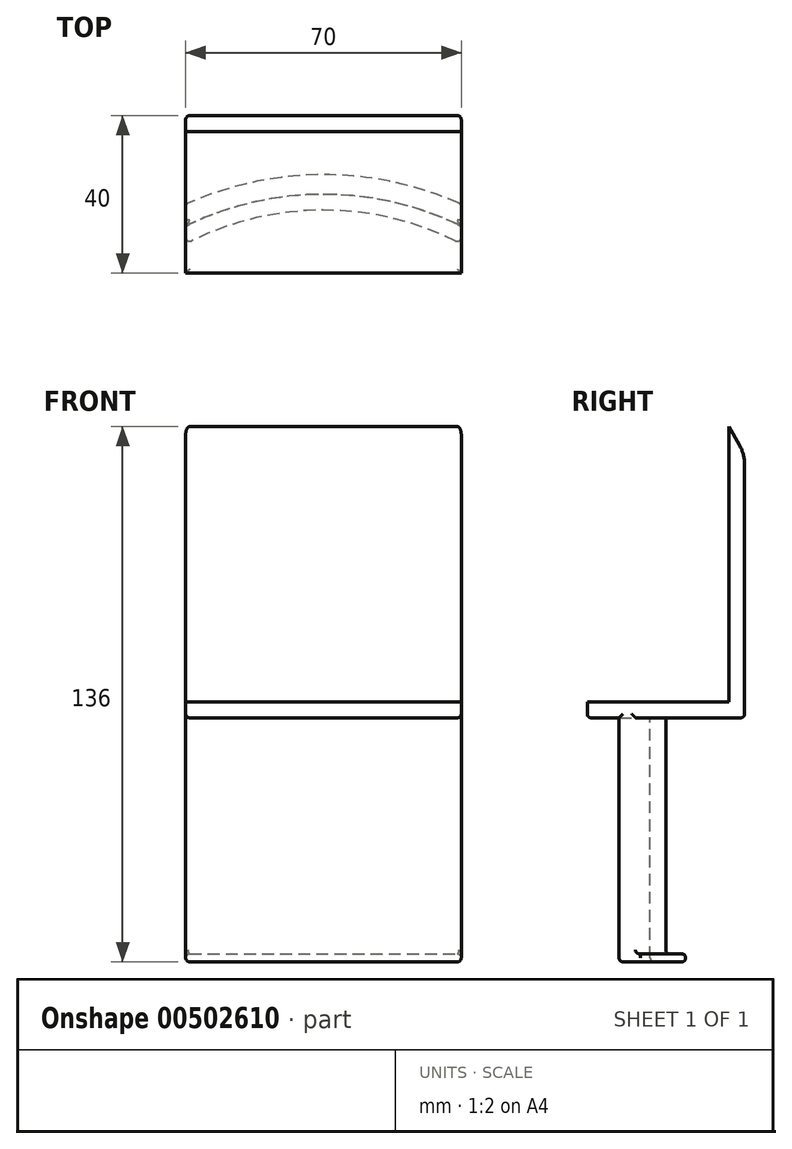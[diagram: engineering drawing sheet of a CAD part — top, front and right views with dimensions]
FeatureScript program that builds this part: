
annotation { "Feature Type Name" : "Feature", "Feature Type Description" : "" }
export const myFeature = defineFeature(function(context is Context, id is Id, definition is map)
    precondition{}
    {
        {
            var Q0;
            Q0=qCreatedBy(makeId("Top.planeOp"),FACE);
            var sketch = newSketch(context, id + "F0", { "sketchPlane" : qUnion([Q0])});
            skLineSegment(sketch, "E0.bottom", {"start": v(-35, 0) * mm, "end": v(35, 0) * mm});
            skLineSegment(sketch, "E0.top", {"start": v(-35, 4) * mm, "end": v(35, 4) * mm});
            skLineSegment(sketch, "E0.left", {"start": v(-35, 0) * mm, "end": v(-35, 4) * mm});
            skLineSegment(sketch, "E0.right", {"start": v(35, 0) * mm, "end": v(35, 4) * mm});
            skSolve(sketch);
        }
        {
            var Q0;
            Q0 = qSketchRegion(id + "F0", true);
            extrude(context, id + "F1", {"entities" : qUnion([Q0]), "depth" : 70 * mm});
        }
        {
            var Q0;
            Q0=makeQuery(id+"F1.opExtrude","CAP_EDGE",EDGE,{"disambiguationData":[OSD([sQuery(id+"F0.wireOp",EDGE,"E0.top")])],"isStart":false});
            chamfer(context, id + "F2", {"entities" : qUnion([Q0]), "chamferType" : ChamferType.TWO_OFFSETS, "width1" : 7 * mm, "oppositeDirection" : false, "width2" : 4 * mm, "tangentPropagation" : true});
        }
        {
            var Q0;
            {var subQ0=sQuery(id+"F0.wireOp",EDGE,"E0.top");Q0=makeQuery(id+"F2.opChamfer","BLEND_EDGE",EDGE,{"blendedFrom":[makeQuery(id+"F1.opExtrude","CAP_EDGE",EDGE,{"disambiguationData":[OSD([subQ0])],"isStart":false}),makeQuery(id+"F1.opExtrude","SWEPT_FACE",FACE,{"disambiguationData":[OSD([subQ0])]})],"blendedInto":[makeQuery(id+"F1.opExtrude","SWEPT_FACE",FACE,{"disambiguationData":[OSD([subQ0])]})]});}
            fillet(context, id + "F3", {"entities" : qUnion([Q0]), "radius" : 10 * mm, "tangentPropagation" : true, "allowEdgeOverflow" : false});
        }
        {
            var Q0;
            Q0=qCreatedBy(makeId("Top.planeOp"),FACE);
            var sketch = newSketch(context, id + "F4", { "sketchPlane" : qUnion([Q0])});
            skPoint(sketch, "E1.0", {"position": v(-35, 4) * mm});
            skPoint(sketch, "E1.1", {"position": v(35, 4) * mm});
            skLineSegment(sketch, "E2.bottom", {"start": v(-35, 4) * mm, "end": v(35, 4) * mm});
            skLineSegment(sketch, "E2.top", {"start": v(-35, -36) * mm, "end": v(35, -36) * mm});
            skLineSegment(sketch, "E2.left", {"start": v(-35, 4) * mm, "end": v(-35, -36) * mm});
            skLineSegment(sketch, "E2.right", {"start": v(35, 4) * mm, "end": v(35, -36) * mm});
            skSolve(sketch);
        }
        {
            var Q0;
            Q0 = qSketchRegion(id + "F4", true);
            extrude(context, id + "F5", {"entities" : qUnion([Q0]), "operationType" : NewBodyOperationType.ADD, "oppositeDirection" : true, "depth" : 4 * mm});
        }
        {
            var Q0;
            Q0=makeQuery(id+"F5.opExtrude","CAP_FACE",FACE,{"disambiguationData":[OSD([sQuery(id+"F4.wireOp",EDGE,"E2.bottom"),sQuery(id+"F4.wireOp",EDGE,"E2.top"),sQuery(id+"F4.wireOp",EDGE,"E2.left"),sQuery(id+"F4.wireOp",EDGE,"E2.right")])],"isStart":false});
            var sketch = newSketch(context, id + "F6", { "sketchPlane" : qUnion([Q0])});
            skArc(sketch, "E3", {"start": v(-35, 24.06) * mm, "mid": v(0, 16) * mm, "end": v(35, 24.06) * mm});
            skArc(sketch, "E4", {"start": v(-35, 28.54) * mm, "mid": v(0, 20) * mm, "end": v(35, 28.54) * mm});
            skLineSegment(sketch, "E5", {"start": v(-35, 28.54) * mm, "end": v(-35, 24.06) * mm});
            skLineSegment(sketch, "E6", {"start": v(35, 28.54) * mm, "end": v(35, 24.06) * mm});
            skSolve(sketch);
        }
        {
            var Q0;
            Q0 = qSketchRegion(id + "F6", true);
            extrude(context, id + "F7", {"entities" : qUnion([Q0]), "operationType" : NewBodyOperationType.ADD, "depth" : 60 * mm});
        }
        {
            var Q0;
            Q0=makeQuery(id+"F7.opExtrude","CAP_FACE",FACE,{"disambiguationData":[OSD([sQuery(id+"F6.wireOp",EDGE,"E3"),sQuery(id+"F6.wireOp",EDGE,"E4"),sQuery(id+"F6.wireOp",EDGE,"E5"),sQuery(id+"F6.wireOp",EDGE,"E6")])],"isStart":false});
            var sketch = newSketch(context, id + "F8", { "sketchPlane" : qUnion([Q0])});
            skArc(sketch, "E7", {"start": v(-35, 18.54) * mm, "mid": v(0, 11) * mm, "end": v(35, 18.54) * mm});
            skLineSegment(sketch, "E8", {"start": v(-35, 24.06) * mm, "end": v(-35, 18.54) * mm});
            skLineSegment(sketch, "E9", {"start": v(35, 24.06) * mm, "end": v(35, 18.54) * mm});
            skLineSegment(sketch, "E10.0", {"start": v(-35, 28.54) * mm, "end": v(-35, 24.06) * mm});
            skArc(sketch, "E10.1", {"start": v(-35, 28.54) * mm, "mid": v(0, 20) * mm, "end": v(35, 28.54) * mm});
            skLineSegment(sketch, "E10.2", {"start": v(35, 28.54) * mm, "end": v(35, 24.06) * mm});
            skSolve(sketch);
        }
        {
            var Q0;
            Q0 = qSketchRegion(id + "F8", true);
            extrude(context, id + "F9", {"entities" : qUnion([Q0]), "operationType" : NewBodyOperationType.ADD, "depth" : 2 * mm});
        }
        {
            var Q0;
            Q0=makeQuery(id+"F7.opExtrude","CAP_EDGE",EDGE,{"disambiguationData":[OSD([sQuery(id+"F6.wireOp",EDGE,"E3")])],"isStart":false});
            var Q1;
            Q1=makeQuery(id+"F7.opExtrude","CAP_EDGE",EDGE,{"disambiguationData":[OSD([sQuery(id+"F6.wireOp",EDGE,"E3")])],"isStart":true});
            var Q2;
            Q2=makeQuery(id+"F5.opExtrude","CAP_EDGE",EDGE,{"disambiguationData":[OSD([sQuery(id+"F4.wireOp",EDGE,"E2.right")])],"isStart":false});
            var Q3;
            Q3=makeQuery(id+"F5.opExtrude","CAP_EDGE",EDGE,{"disambiguationData":[OSD([sQuery(id+"F4.wireOp",EDGE,"E2.left")])],"isStart":false});
            var Q4;
            Q4=makeQuery(id+"F5.opExtrude","CAP_EDGE",EDGE,{"disambiguationData":[OSD([sQuery(id+"F4.wireOp",EDGE,"E2.top")])],"isStart":false});
            var Q5;
            Q5=makeQuery(id+"F9.opExtrude","CAP_EDGE",EDGE,{"disambiguationData":[OSD([sQuery(id+"F8.wireOp",EDGE,"E10.1")])],"isStart":false});
            var Q6;
            Q6=makeQuery(id+"F9.boolean.opBoolean","MERGE",EDGE,{"derivedFrom":[makeQuery(id+"F7.opExtrude","SWEPT_EDGE",EDGE,{"disambiguationData":[OSD([sQuery(id+"F6.wireOp",EDGE,"E4"),sQuery(id+"F6.wireOp",EDGE,"E6")])]}),makeQuery(id+"F9.opExtrude","SWEPT_EDGE",EDGE,{"disambiguationData":[OSD([sQuery(id+"F8.wireOp",EDGE,"E10.1"),sQuery(id+"F8.wireOp",EDGE,"E10.2")])]})]});
            var Q7;
            Q7=makeQuery(id+"F9.boolean.opBoolean","MERGE",EDGE,{"derivedFrom":[makeQuery(id+"F7.opExtrude","SWEPT_EDGE",EDGE,{"disambiguationData":[OSD([sQuery(id+"F6.wireOp",EDGE,"E4"),sQuery(id+"F6.wireOp",EDGE,"E5")])]}),makeQuery(id+"F9.opExtrude","SWEPT_EDGE",EDGE,{"disambiguationData":[OSD([sQuery(id+"F8.wireOp",EDGE,"E10.0"),sQuery(id+"F8.wireOp",EDGE,"E10.1")])]})]});
            var Q8;
            Q8=makeQuery(id+"F7.opExtrude","SWEPT_EDGE",EDGE,{"disambiguationData":[OSD([sQuery(id+"F6.wireOp",EDGE,"E3"),sQuery(id+"F6.wireOp",EDGE,"E5")])]});
            var Q9;
            Q9=makeQuery(id+"F7.opExtrude","SWEPT_EDGE",EDGE,{"disambiguationData":[OSD([sQuery(id+"F6.wireOp",EDGE,"E3"),sQuery(id+"F6.wireOp",EDGE,"E6")])]});
            var Q10;
            Q10=makeQuery(id+"F9.opExtrude","CAP_EDGE",EDGE,{"disambiguationData":[OSD([sQuery(id+"F8.wireOp",EDGE,"E7")])],"isStart":false});
            var Q11;
            Q11=makeQuery(id+"F9.opExtrude","CAP_EDGE",EDGE,{"disambiguationData":[OSD([sQuery(id+"F8.wireOp",EDGE,"E7")])],"isStart":true});
            var Q12;
            Q12=makeQuery(id+"F9.opExtrude","CAP_EDGE",EDGE,{"disambiguationData":[OSD([sQuery(id+"F8.wireOp",EDGE,"E9"),sQuery(id+"F8.wireOp",EDGE,"E10.2")])],"isStart":false});
            var Q13;
            Q13=makeQuery(id+"F9.opExtrude","CAP_EDGE",EDGE,{"disambiguationData":[OSD([sQuery(id+"F8.wireOp",EDGE,"E8"),sQuery(id+"F8.wireOp",EDGE,"E10.0")])],"isStart":false});
            var Q14;
            Q14=makeQuery(id+"F9.opExtrude","CAP_EDGE",EDGE,{"disambiguationData":[OSD([sQuery(id+"F8.wireOp",EDGE,"E8"),sQuery(id+"F8.wireOp",EDGE,"E10.0")])],"isStart":true});
            var Q15;
            Q15=makeQuery(id+"F9.opExtrude","SWEPT_EDGE",EDGE,{"disambiguationData":[OSD([sQuery(id+"F8.wireOp",EDGE,"E7"),sQuery(id+"F8.wireOp",EDGE,"E9")])]});
            var Q16;
            Q16=makeQuery(id+"F9.opExtrude","CAP_EDGE",EDGE,{"disambiguationData":[OSD([sQuery(id+"F8.wireOp",EDGE,"E9"),sQuery(id+"F8.wireOp",EDGE,"E10.2")])],"isStart":true});
            var Q17;
            Q17=makeQuery(id+"F9.opExtrude","SWEPT_EDGE",EDGE,{"disambiguationData":[OSD([sQuery(id+"F8.wireOp",EDGE,"E7"),sQuery(id+"F8.wireOp",EDGE,"E8")])]});
            var Q18;
            Q18=makeQuery(id+"F5.opExtrude","CAP_EDGE",EDGE,{"disambiguationData":[OSD([sQuery(id+"F4.wireOp",EDGE,"E2.bottom")])],"isStart":false});
            var Q19;
            Q19=makeQuery(id+"F5.boolean.opBoolean","MERGE",EDGE,{"derivedFrom":[makeQuery(id+"F1.opExtrude","SWEPT_EDGE",EDGE,{"disambiguationData":[OSD([sQuery(id+"F0.wireOp",EDGE,"E0.top"),sQuery(id+"F0.wireOp",EDGE,"E0.right")])]}),makeQuery(id+"F5.opExtrude","SWEPT_EDGE",EDGE,{"disambiguationData":[OSD([sQuery(id+"F4.wireOp",EDGE,"E2.bottom"),sQuery(id+"F4.wireOp",EDGE,"E2.right")])]})]});
            var Q20;
            Q20=makeQuery(id+"F5.boolean.opBoolean","MERGE",EDGE,{"derivedFrom":[makeQuery(id+"F1.opExtrude","SWEPT_EDGE",EDGE,{"disambiguationData":[OSD([sQuery(id+"F0.wireOp",EDGE,"E0.top"),sQuery(id+"F0.wireOp",EDGE,"E0.left")])]}),makeQuery(id+"F5.opExtrude","SWEPT_EDGE",EDGE,{"disambiguationData":[OSD([sQuery(id+"F4.wireOp",EDGE,"E2.bottom"),sQuery(id+"F4.wireOp",EDGE,"E2.left")])]})]});
            fillet(context, id + "F10", {"entities" : qUnion([Q0, Q1, Q2, Q3, Q4, Q5, Q6, Q7, Q8, Q9, Q10, Q11, Q12, Q13, Q14, Q15, Q16, Q17, Q18, Q19, Q20]), "radius" : 1 * mm, "tangentPropagation" : true, "allowEdgeOverflow" : false});
        }
    });
